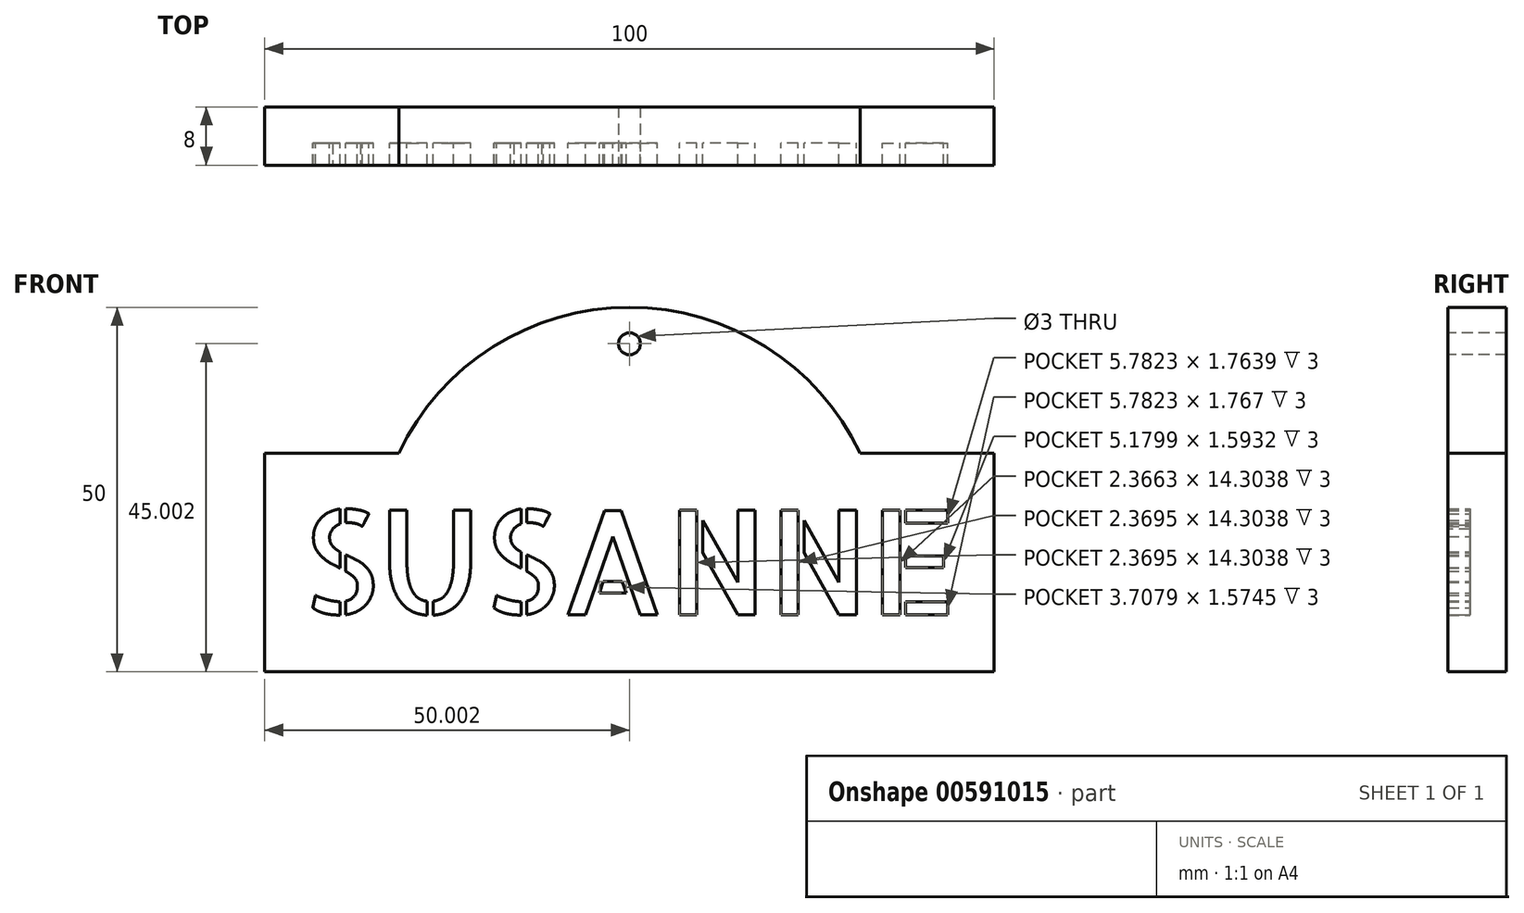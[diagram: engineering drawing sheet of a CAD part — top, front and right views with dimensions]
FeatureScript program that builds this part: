
annotation { "Feature Type Name" : "Feature", "Feature Type Description" : "" }
export const myFeature = defineFeature(function(context is Context, id is Id, definition is map)
    precondition{}
    {
        {
            var Q0;
            Q0=qCreatedBy(makeId("Front.planeOp"),FACE);
            var sketch = newSketch(context, id + "F0", { "sketchPlane" : qUnion([Q0])});
            skLineSegment(sketch, "E0.bottom", {"start": v(-55.8, 41.64) * mm, "end": v(-37.42, 41.64) * mm});
            skLineSegment(sketch, "E0.top", {"start": v(-55.8, 11.64) * mm, "end": v(44.2, 11.64) * mm});
            skLineSegment(sketch, "E0.left", {"start": v(-55.8, 41.64) * mm, "end": v(-55.8, 11.64) * mm});
            skLineSegment(sketch, "E0.right", {"start": v(44.2, 41.64) * mm, "end": v(44.2, 11.64) * mm});
            skArc(sketch, "E1", {"start": v(25.83, 41.64) * mm, "mid": v(-5.8, 61.64) * mm, "end": v(-37.42, 41.64) * mm});
            skPoint(sketch, "E2", {"position": v(-5.8, 11.64) * mm});
            skPoint(sketch, "E3", {"position": v(44.2, 26.64) * mm});
            skCircle(sketch, "E4", {"center": v(-5.8, 56.64) * mm, "radius": 1.5 * mm});
            skText(sketch, "E5", { "text": "SUSANNE", "fontName": "AllertaStencil-Regular.ttf"});
            skPoint(sketch, "E6", {"position": v(-55.8, 26.64) * mm});
            skPoint(sketch, "E7", {"position": v(-50.8, 26.64) * mm});
            skLineSegment(sketch, "E8.trimOffspring", {"start": v(25.83, 41.64) * mm, "end": v(44.2, 41.64) * mm});
            const initialGuessF0  = {"E5": [-0.0508, 0.01949, 1, 0, 0.01431]};
            skSetInitialGuess(sketch, initialGuessF0);
            skSolve(sketch);
        }
        {
            var Q0;
            Q0=makeQuery(id+"F0.imprint","IMPRINT",FACE,{"disambiguationData":[TD([[makeQuery(id+"F0.imprint","IMPRINT",EDGE,{"derivedFrom":sQuery(id+"F0.wireOp",EDGE,"E0.bottom")}),-1.0]])]});
            var Q1;
            Q1=makeQuery(id+"F0.imprint","IMPRINT",FACE,{"disambiguationData":[TD([[makeQuery(id+"F0.imprint","IMPRINT",EDGE,{"derivedFrom":sQuery(id+"F0.wireOp",EDGE,"E5.sketch_text.stroke-0")}),-1.0]])]});
            var Q2;
            Q2=makeQuery(id+"F0.imprint","IMPRINT",FACE,{"disambiguationData":[TD([[makeQuery(id+"F0.imprint","IMPRINT",EDGE,{"derivedFrom":sQuery(id+"F0.wireOp",EDGE,"E5.sketch_text.stroke-11")}),-1.0]])]});
            var Q3;
            Q3=makeQuery(id+"F0.imprint","IMPRINT",FACE,{"disambiguationData":[TD([[makeQuery(id+"F0.imprint","IMPRINT",EDGE,{"derivedFrom":sQuery(id+"F0.wireOp",EDGE,"E5.sketch_text.stroke-37")}),-1.0]])]});
            var Q4;
            Q4=makeQuery(id+"F0.imprint","IMPRINT",FACE,{"disambiguationData":[TD([[makeQuery(id+"F0.imprint","IMPRINT",EDGE,{"derivedFrom":sQuery(id+"F0.wireOp",EDGE,"E5.sketch_text.stroke-25")}),-1.0]])]});
            var Q5;
            Q5=makeQuery(id+"F0.imprint","IMPRINT",FACE,{"disambiguationData":[TD([[makeQuery(id+"F0.imprint","IMPRINT",EDGE,{"derivedFrom":sQuery(id+"F0.wireOp",EDGE,"E5.sketch_text.stroke-50")}),-1.0]])]});
            var Q6;
            Q6=makeQuery(id+"F0.imprint","IMPRINT",FACE,{"disambiguationData":[TD([[makeQuery(id+"F0.imprint","IMPRINT",EDGE,{"derivedFrom":sQuery(id+"F0.wireOp",EDGE,"E5.sketch_text.stroke-62")}),-1.0]])]});
            var Q7;
            Q7=makeQuery(id+"F0.imprint","IMPRINT",FACE,{"disambiguationData":[TD([[makeQuery(id+"F0.imprint","IMPRINT",EDGE,{"derivedFrom":sQuery(id+"F0.wireOp",EDGE,"E5.sketch_text.stroke-85")}),-1.0]])]});
            var Q8;
            Q8=makeQuery(id+"F0.imprint","IMPRINT",FACE,{"disambiguationData":[TD([[makeQuery(id+"F0.imprint","IMPRINT",EDGE,{"derivedFrom":sQuery(id+"F0.wireOp",EDGE,"E5.sketch_text.stroke-74")}),-1.0]])]});
            var Q9;
            Q9=makeQuery(id+"F0.imprint","IMPRINT",FACE,{"disambiguationData":[TD([[makeQuery(id+"F0.imprint","IMPRINT",EDGE,{"derivedFrom":sQuery(id+"F0.wireOp",EDGE,"E5.sketch_text.stroke-111")}),-1.0]])]});
            var Q10;
            Q10=makeQuery(id+"F0.imprint","IMPRINT",FACE,{"disambiguationData":[TD([[makeQuery(id+"F0.imprint","IMPRINT",EDGE,{"derivedFrom":sQuery(id+"F0.wireOp",EDGE,"E5.sketch_text.stroke-99")}),-1.0]])]});
            var Q11;
            Q11=makeQuery(id+"F0.imprint","IMPRINT",FACE,{"disambiguationData":[TD([[makeQuery(id+"F0.imprint","IMPRINT",EDGE,{"derivedFrom":sQuery(id+"F0.wireOp",EDGE,"E5.sketch_text.stroke-124")}),-1.0]])]});
            var Q12;
            Q12=makeQuery(id+"F0.imprint","IMPRINT",FACE,{"disambiguationData":[TD([[makeQuery(id+"F0.imprint","IMPRINT",EDGE,{"derivedFrom":sQuery(id+"F0.wireOp",EDGE,"E5.sketch_text.stroke-131")}),-1.0]])]});
            var Q13;
            Q13=makeQuery(id+"F0.imprint","IMPRINT",FACE,{"disambiguationData":[TD([[makeQuery(id+"F0.imprint","IMPRINT",EDGE,{"derivedFrom":sQuery(id+"F0.wireOp",EDGE,"E5.sketch_text.stroke-142")}),-1.0]])]});
            var Q14;
            Q14=makeQuery(id+"F0.imprint","IMPRINT",FACE,{"disambiguationData":[TD([[makeQuery(id+"F0.imprint","IMPRINT",EDGE,{"derivedFrom":sQuery(id+"F0.wireOp",EDGE,"E5.sketch_text.stroke-135")}),-1.0]])]});
            var Q15;
            Q15=makeQuery(id+"F0.imprint","IMPRINT",FACE,{"disambiguationData":[TD([[makeQuery(id+"F0.imprint","IMPRINT",EDGE,{"derivedFrom":sQuery(id+"F0.wireOp",EDGE,"E5.sketch_text.stroke-153")}),-1.0]])]});
            var Q16;
            Q16=makeQuery(id+"F0.imprint","IMPRINT",FACE,{"disambiguationData":[TD([[makeQuery(id+"F0.imprint","IMPRINT",EDGE,{"derivedFrom":sQuery(id+"F0.wireOp",EDGE,"E5.sketch_text.stroke-146")}),-1.0]])]});
            var Q17;
            Q17=makeQuery(id+"F0.imprint","IMPRINT",FACE,{"disambiguationData":[TD([[makeQuery(id+"F0.imprint","IMPRINT",EDGE,{"derivedFrom":sQuery(id+"F0.wireOp",EDGE,"E5.sketch_text.stroke-157")}),-1.0]])]});
            var Q18;
            Q18=makeQuery(id+"F0.imprint","IMPRINT",FACE,{"disambiguationData":[TD([[makeQuery(id+"F0.imprint","IMPRINT",EDGE,{"derivedFrom":sQuery(id+"F0.wireOp",EDGE,"E5.sketch_text.stroke-169")}),-1.0]])]});
            var Q19;
            Q19=makeQuery(id+"F0.imprint","IMPRINT",FACE,{"disambiguationData":[TD([[makeQuery(id+"F0.imprint","IMPRINT",EDGE,{"derivedFrom":sQuery(id+"F0.wireOp",EDGE,"E5.sketch_text.stroke-161")}),-1.0]])]});
            var Q20;
            Q20=makeQuery(id+"F0.imprint","IMPRINT",FACE,{"disambiguationData":[TD([[makeQuery(id+"F0.imprint","IMPRINT",EDGE,{"derivedFrom":sQuery(id+"F0.wireOp",EDGE,"E5.sketch_text.stroke-165")}),-1.0]])]});
            extrude(context, id + "F1", {"entities" : qUnion([Q0, Q1, Q2, Q3, Q4, Q5, Q6, Q7, Q8, Q9, Q10, Q11, Q12, Q13, Q14, Q15, Q16, Q17, Q18, Q19, Q20]), "oppositeDirection" : true, "depth" : 5 * mm, "offsetDistance" : 25 * mm});
        }
        {
            var Q0;
            Q0=makeQuery(id+"F0.imprint","IMPRINT",FACE,{"disambiguationData":[TD([[makeQuery(id+"F0.imprint","IMPRINT",EDGE,{"derivedFrom":sQuery(id+"F0.wireOp",EDGE,"E0.bottom")}),-1.0]])]});
            extrude(context, id + "F2", {"entities" : qUnion([Q0]), "operationType" : NewBodyOperationType.ADD, "depth" : 3 * mm, "offsetDistance" : 25 * mm});
        }
    });
